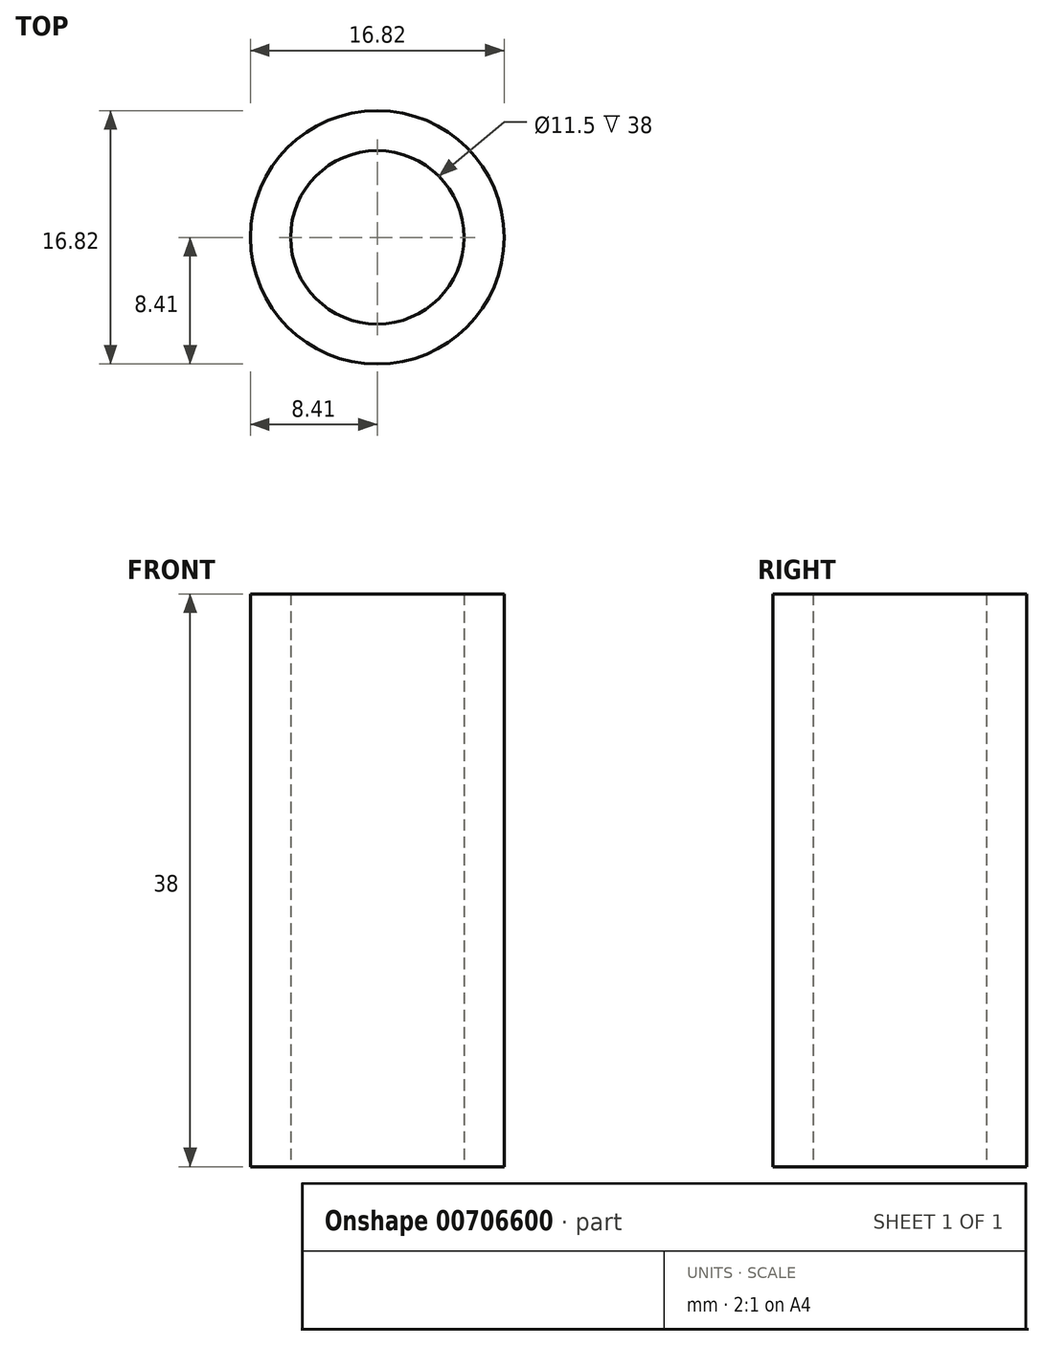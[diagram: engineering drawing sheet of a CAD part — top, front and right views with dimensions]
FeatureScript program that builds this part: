
annotation { "Feature Type Name" : "Feature", "Feature Type Description" : "" }
export const myFeature = defineFeature(function(context is Context, id is Id, definition is map)
    precondition{}
    {
        {
            var Q0;
            Q0=qCreatedBy(makeId("Top.planeOp"),FACE);
            var sketch = newSketch(context, id + "F0", { "sketchPlane" : qUnion([Q0])});
            skCircle(sketch, "E0", {"center": v(0, 0) * mm, "radius": 8.4 * mm});
            skCircle(sketch, "E1", {"center": v(0, 0) * mm, "radius": 5.75 * mm});
            skSolve(sketch);
        }
        {
            var Q0;
            Q0=makeQuery(id+"F0.imprint","IMPRINT",FACE,{"disambiguationData":[TD([[makeQuery(id+"F0.imprint","IMPRINT",EDGE,{"derivedFrom":sQuery(id+"F0.wireOp",EDGE,"E0")}),1.0]])]});
            extrude(context, id + "F1", {"entities" : qUnion([Q0]), "depth" : 38 * mm, "offsetDistance" : 25.4 * mm});
        }
    });
